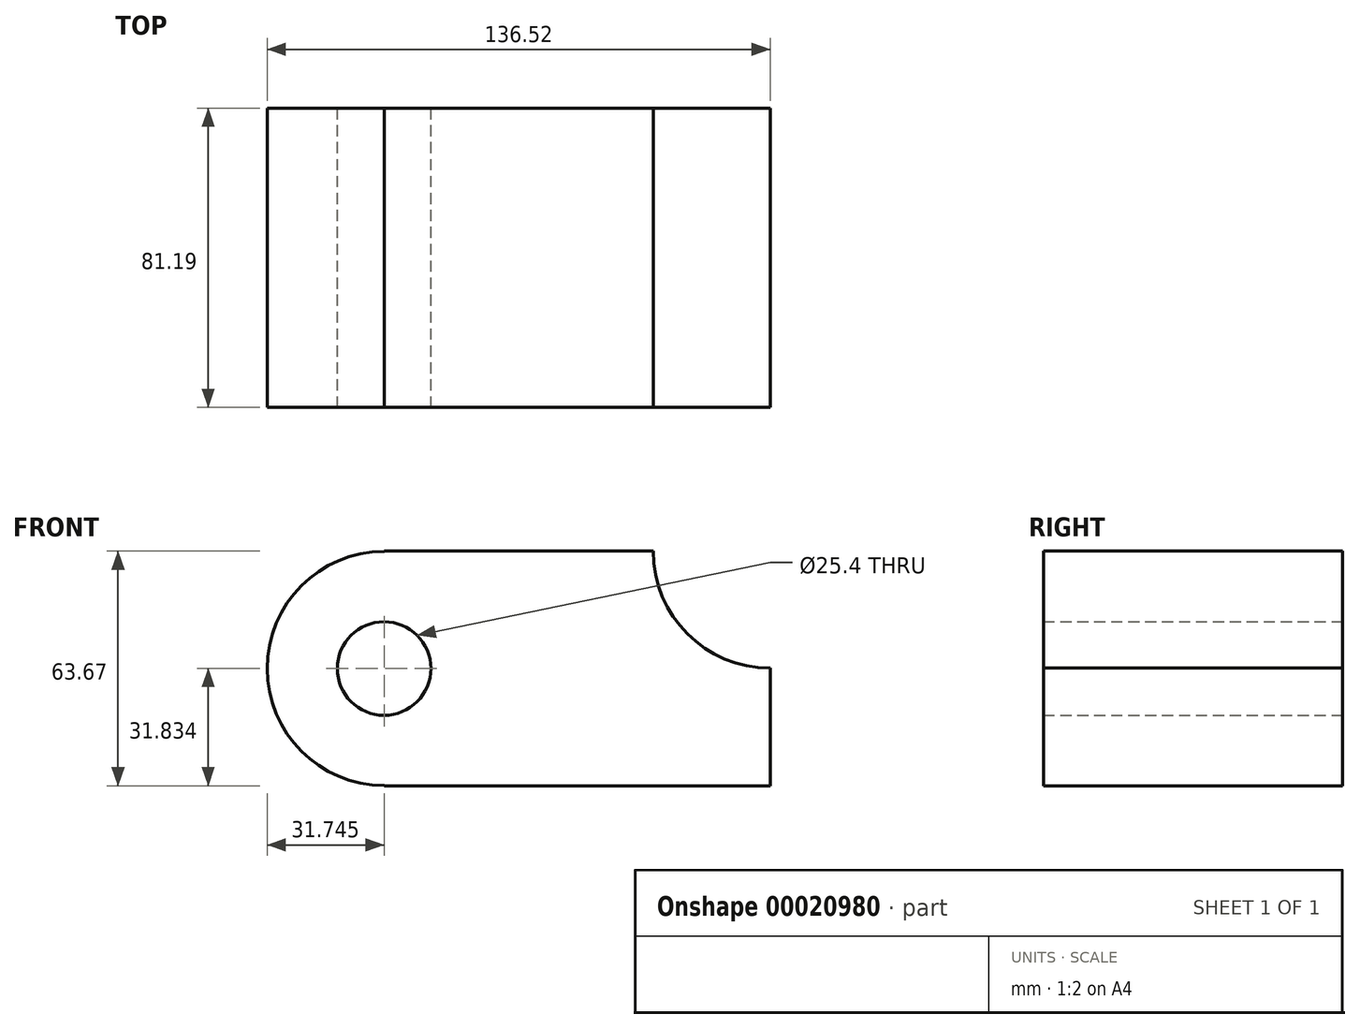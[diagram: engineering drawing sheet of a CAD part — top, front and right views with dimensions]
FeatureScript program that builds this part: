
annotation { "Feature Type Name" : "Feature", "Feature Type Description" : "" }
export const myFeature = defineFeature(function(context is Context, id is Id, definition is map)
    precondition{}
    {
        {
            var Q0;
            Q0=qCreatedBy(makeId("Front.planeOp"),FACE);
            var sketch = newSketch(context, id + "F0", { "sketchPlane" : qUnion([Q0])});
            skLineSegment(sketch, "E0.bottom", {"start": v(0, 0) * mm, "end": v(-104.78, 0) * mm});
            skLineSegment(sketch, "E0.top", {"start": v(-31.75, 63.67) * mm, "end": v(-104.78, 63.67) * mm});
            skLineSegment(sketch, "E0.left", {"start": v(0, 0) * mm, "end": v(0, 31.92) * mm});
            skLineSegment(sketch, "E0.right", {"start": v(-104.78, 0) * mm, "end": v(-104.78, 0.08) * mm});
            skArc(sketch, "E1", {"start": v(-104.78, 63.58) * mm, "mid": v(-136.53, 31.83) * mm, "end": v(-104.78, 0.08) * mm});
            skCircle(sketch, "E2", {"center": v(-104.78, 31.83) * mm, "radius": 12.7 * mm});
            skArc(sketch, "E3", {"start": v(-31.75, 63.67) * mm, "mid": v(-22.45, 41.22) * mm, "end": v(0, 31.92) * mm});
            skLineSegment(sketch, "E4.trimOffspring", {"start": v(-104.78, 63.58) * mm, "end": v(-104.78, 63.67) * mm});
            skSolve(sketch);
        }
        {
            var Q0;
            Q0 = qSketchRegion(id + "F0", true);
            extrude(context, id + "F1", {"entities" : qUnion([Q0]), "depth" : 55.8 * mm});
        }
        {
            var Q0;
            Q0=makeQuery(id+"F1.opExtrude","CAP_FACE",FACE,{"disambiguationData":[OSD([sQuery(id+"F0.wireOp",EDGE,"E0.bottom"),sQuery(id+"F0.wireOp",EDGE,"E0.top"),sQuery(id+"F0.wireOp",EDGE,"E0.left"),sQuery(id+"F0.wireOp",EDGE,"E0.right"),sQuery(id+"F0.wireOp",EDGE,"E1"),sQuery(id+"F0.wireOp",EDGE,"E2"),sQuery(id+"F0.wireOp",EDGE,"E3"),sQuery(id+"F0.wireOp",EDGE,"E4.trimOffspring")])],"isStart":true});
            var Q1;
            Q1=makeQuery(id+"F1.opExtrude","CAP_FACE",FACE,{"disambiguationData":[OSD([sQuery(id+"F0.wireOp",EDGE,"E0.bottom"),sQuery(id+"F0.wireOp",EDGE,"E0.top"),sQuery(id+"F0.wireOp",EDGE,"E0.left"),sQuery(id+"F0.wireOp",EDGE,"E0.right"),sQuery(id+"F0.wireOp",EDGE,"E1"),sQuery(id+"F0.wireOp",EDGE,"E2"),sQuery(id+"F0.wireOp",EDGE,"E3"),sQuery(id+"F0.wireOp",EDGE,"E4.trimOffspring")])],"isStart":false});
            extrude(context, id + "F2", {"entities" : qUnion([Q0, Q1]), "operationType" : NewBodyOperationType.ADD, "oppositeDirection" : true, "depth" : 25.4 * mm});
        }
    });
